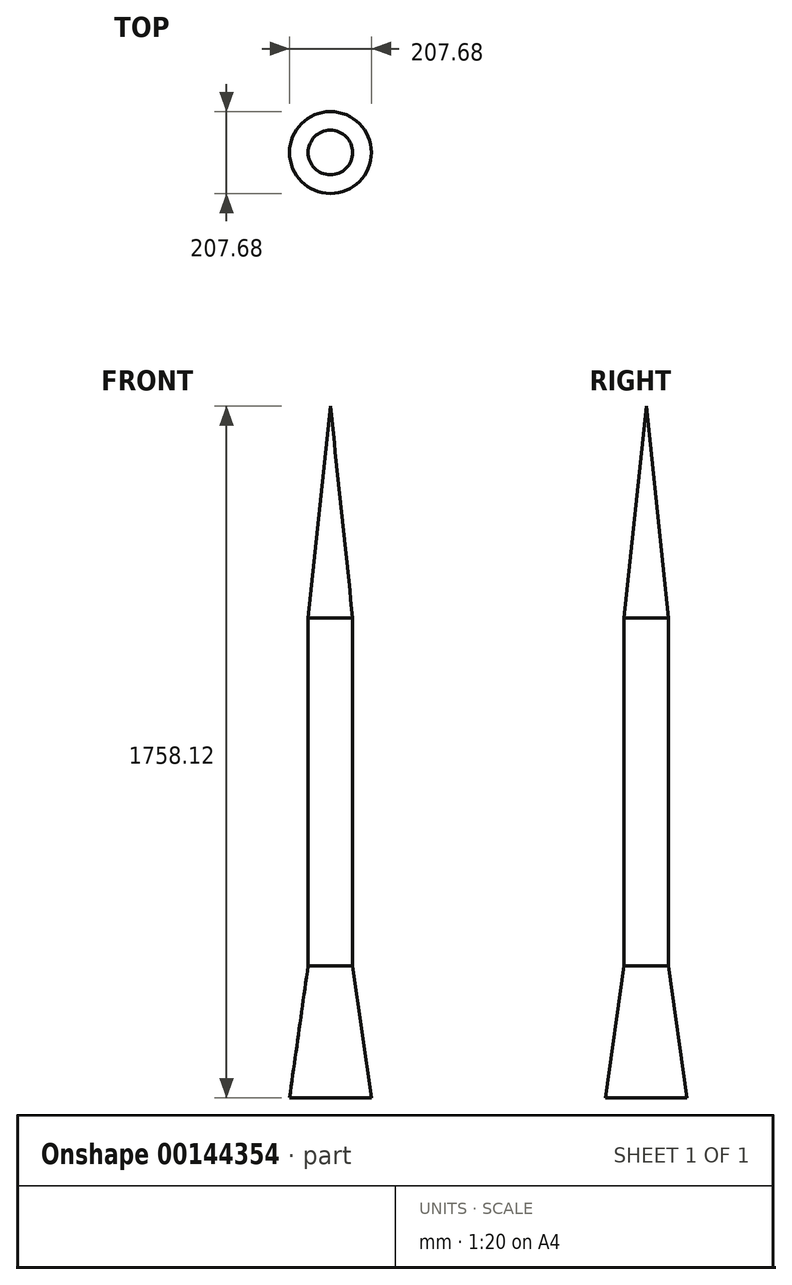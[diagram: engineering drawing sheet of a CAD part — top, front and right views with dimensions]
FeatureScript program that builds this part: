
annotation { "Feature Type Name" : "Feature", "Feature Type Description" : "" }
export const myFeature = defineFeature(function(context is Context, id is Id, definition is map)
    precondition{}
    {
        {
            var Q0;
            Q0=qCreatedBy(makeId("Top.planeOp"),FACE);
            var sketch = newSketch(context, id + "F0", { "sketchPlane" : qUnion([Q0])});
            skCircle(sketch, "E0", {"center": v(0, 0) * mm, "radius": 56.64 * mm});
            skSolve(sketch);
        }
        {
            var Q0;
            Q0=makeQuery(id+"F0.imprint","IMPRINT",FACE,{"disambiguationData":[TD([[makeQuery(id+"F0.imprint","IMPRINT",EDGE,{"derivedFrom":sQuery(id+"F0.wireOp",EDGE,"E0")}),1.0]])]});
            extrude(context, id + "F1", {"entities" : qUnion([Q0]), "oppositeDirection" : true, "depth" : 414.36 * mm});
        }
        {
            var Q0;
            Q0=makeQuery(id+"F1.opExtrude","CAP_FACE",FACE,{"disambiguationData":[OSD([sQuery(id+"F0.wireOp",EDGE,"E0")])],"isStart":true});
            var sketch = newSketch(context, id + "F2", { "sketchPlane" : qUnion([Q0])});
            skCircle(sketch, "E1.0", {"center": v(0, 0) * mm, "radius": 56.64 * mm});
            skSolve(sketch);
        }
        {
            var Q0;
            Q0 = qSketchRegion(id + "F2", true);
            extrude(context, id + "F3", {"entities" : qUnion([Q0]), "operationType" : NewBodyOperationType.ADD, "depth" : 25.4 * mm});
        }
        {
            var Q0;
            Q0=makeQuery(id+"F3.opExtrude","CAP_FACE",FACE,{"disambiguationData":[OSD([sQuery(id+"F2.wireOp",EDGE,"E1.0")])],"isStart":false});
            var sketch = newSketch(context, id + "F4", { "sketchPlane" : qUnion([Q0])});
            skCircle(sketch, "E2.0", {"center": v(0, 0) * mm, "radius": 56.64 * mm});
            skSolve(sketch);
        }
        {
            var Q0;
            Q0 = qSketchRegion(id + "F4", true);
            extrude(context, id + "F5", {"entities" : qUnion([Q0]), "operationType" : NewBodyOperationType.ADD, "depth" : 638.02 * mm, "hasDraft" : true, "draftAngle" : 6 * degree, "draftPullDirection" : true});
        }
        {
            var Q0;
            Q0=makeQuery(id+"F1.opExtrude","CAP_FACE",FACE,{"disambiguationData":[OSD([sQuery(id+"F0.wireOp",EDGE,"E0")])],"isStart":false});
            var sketch = newSketch(context, id + "F6", { "sketchPlane" : qUnion([Q0])});
            skCircle(sketch, "E3.0", {"center": v(0, 0) * mm, "radius": 56.64 * mm});
            skSolve(sketch);
        }
        {
            var Q0;
            Q0 = qSketchRegion(id + "F6", true);
            extrude(context, id + "F7", {"entities" : qUnion([Q0]), "operationType" : NewBodyOperationType.ADD, "depth" : 443.62 * mm});
        }
        {
            var Q0;
            Q0=makeQuery(id+"F7.opExtrude","CAP_FACE",FACE,{"disambiguationData":[OSD([sQuery(id+"F6.wireOp",EDGE,"E3.0")])],"isStart":false});
            var sketch = newSketch(context, id + "F8", { "sketchPlane" : qUnion([Q0])});
            skCircle(sketch, "E4.0", {"center": v(0, 0) * mm, "radius": 56.64 * mm});
            skSolve(sketch);
        }
        {
            var Q0;
            Q0 = qSketchRegion(id + "F8", true);
            extrude(context, id + "F9", {"entities" : qUnion([Q0]), "operationType" : NewBodyOperationType.ADD, "depth" : 335.84 * mm, "hasDraft" : true, "draftAngle" : 8 * degree});
        }
    });
